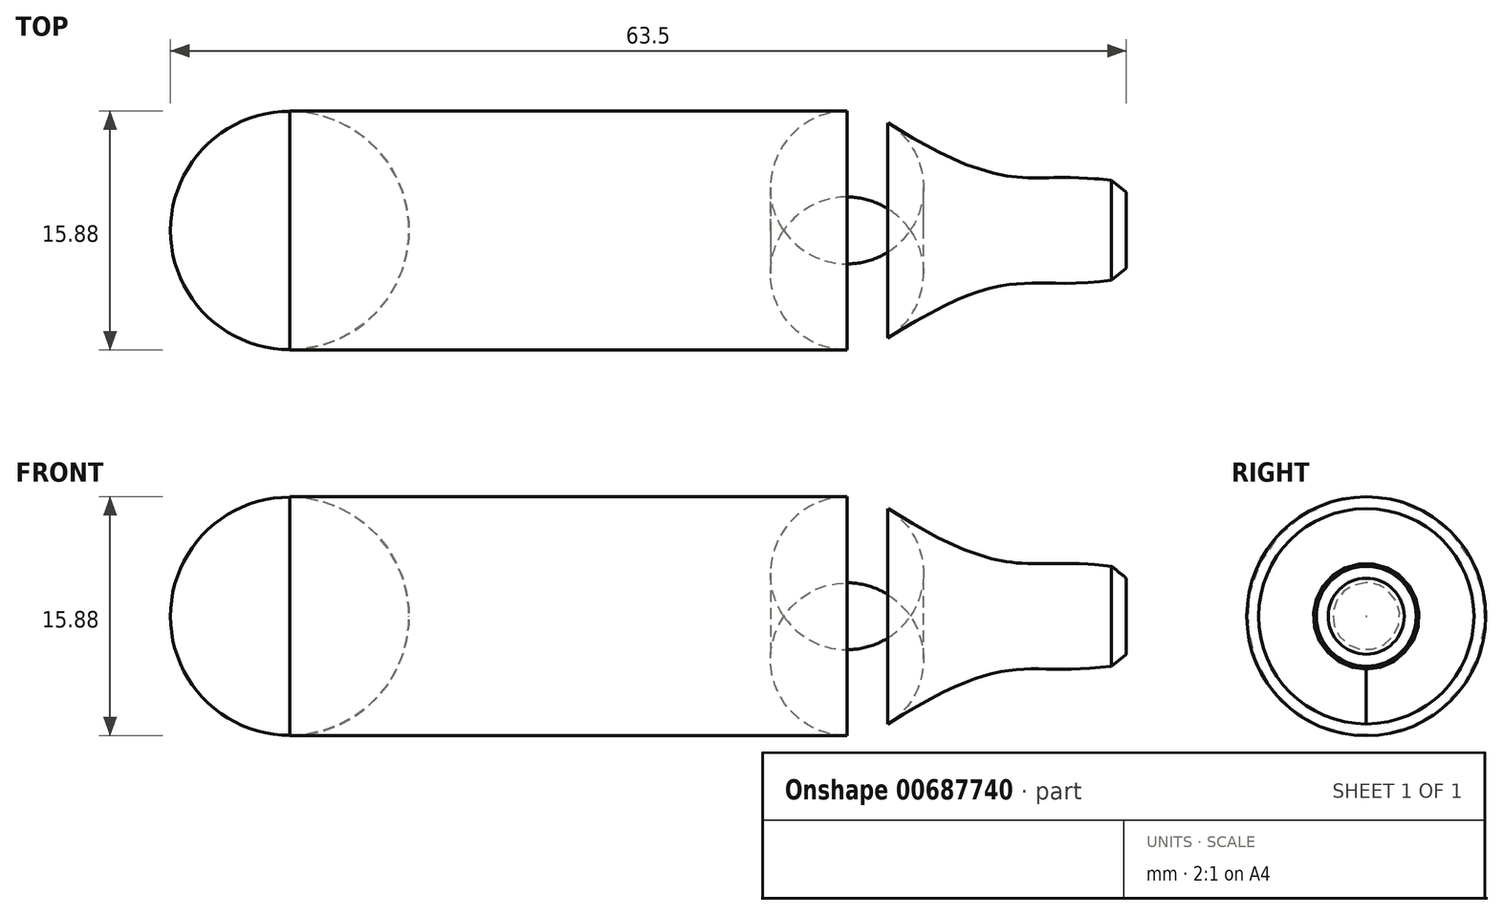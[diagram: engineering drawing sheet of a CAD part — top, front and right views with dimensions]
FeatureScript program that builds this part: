
annotation { "Feature Type Name" : "Feature", "Feature Type Description" : "" }
export const myFeature = defineFeature(function(context is Context, id is Id, definition is map)
    precondition{}
    {
        {
            var Q0;
            Q0=qCreatedBy(makeId("Front.planeOp"),FACE);
            var sketch = newSketch(context, id + "F0", { "sketchPlane" : qUnion([Q0])});
            skLineSegment(sketch, "E0", {"start": v(0, 0) * mm, "end": v(46.44, 0) * mm});
            skFitSpline(sketch, "E1", {"points": [v(46.44, 0) * mm, v(63.5, 4.76) * mm], "startDerivative": vector(29.58, 19.48) * mm, "endDerivative": vector(21.59, 3.6) * mm});
            skLineSegment(sketch, "E2", {"start": v(63.5, 4.76) * mm, "end": v(63.5, 7.94) * mm});
            skLineSegment(sketch, "E3", {"start": v(63.5, 7.94) * mm, "end": v(0, 7.94) * mm});
            skLineSegment(sketch, "E4", {"start": v(0, 7.94) * mm, "end": v(0, 0) * mm});
            skSolve(sketch);
        }
        {
            var Q0;
            Q0=makeQuery(id+"F0.imprint","IMPRINT",FACE,{"disambiguationData":[TD([[makeQuery(id+"F0.imprint","IMPRINT",EDGE,{"derivedFrom":sQuery(id+"F0.wireOp",EDGE,"E0")}),1.0]])]});
            var Q1;
            Q1=sQuery(id+"F0.wireOp",EDGE,"E3");
            revolve(context, id + "F1", {"entities" : qUnion([Q0]), "axis" : qUnion([Q1]), "revolveType" : RevolveType.FULL});
        }
        {
            var Q0;
            Q0=makeQuery(id+"F1.opRevolve","SWEPT_EDGE",EDGE,{"disambiguationData":[OSD([sQuery(id+"F0.wireOp",EDGE,"E0"),sQuery(id+"F0.wireOp",EDGE,"E4")])]});
            fillet(context, id + "F2", {"entities" : qUnion([Q0]), "radius" : 7.92 * mm, "tangentPropagation" : true, "allowEdgeOverflow" : false});
        }
        {
            var Q0;
            Q0=makeQuery(id+"F1.opRevolve","SWEPT_EDGE",EDGE,{"disambiguationData":[OSD([sQuery(id+"F0.wireOp",EDGE,"E0"),sQuery(id+"F0.wireOp",EDGE,"E1")])]});
            fillet(context, id + "F3", {"entities" : qUnion([Q0]), "radius" : 5.08 * mm, "tangentPropagation" : true, "allowEdgeOverflow" : false});
        }
        {
            var Q0;
            Q0=makeQuery(id+"F1.opRevolve","SWEPT_EDGE",EDGE,{"disambiguationData":[OSD([sQuery(id+"F0.wireOp",EDGE,"E1"),sQuery(id+"F0.wireOp",EDGE,"E2")])]});
            chamfer(context, id + "F4", {"entities" : qUnion([Q0]), "chamferType" : ChamferType.OFFSET_ANGLE, "width" : 0.64 * mm, "oppositeDirection" : false, "angle" : 50 * degree, "tangentPropagation" : true});
        }
    });
